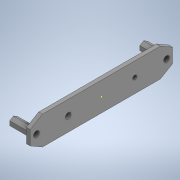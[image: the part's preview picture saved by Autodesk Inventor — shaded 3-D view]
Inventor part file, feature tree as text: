
AUTODESK INVENTOR PART (.ipt)
format: ipt  version: 2020 (Build 240168000, 168)  size: 139,776 bytes
history: native  units: in
note: dims shown in document units (in); Inventor stores cm internally (conversion verified against a paired STEP export)
features: other x3, sketch x1
ambient origin geometry x8: Origin, YZ Plane, XZ Plane, XY Plane, X Axis, Y Axis, Z Axis, Center Point
bodies: Solid1 (feature_tree)
feature tree (4):
  other  "HexWheelGuard.ipt"
  sketch  "Sketch1"  dims[d1=0.3937in]
  other  "Solid1::HexWheelGuard.ipt"
  other  "TaggingFeature2"
